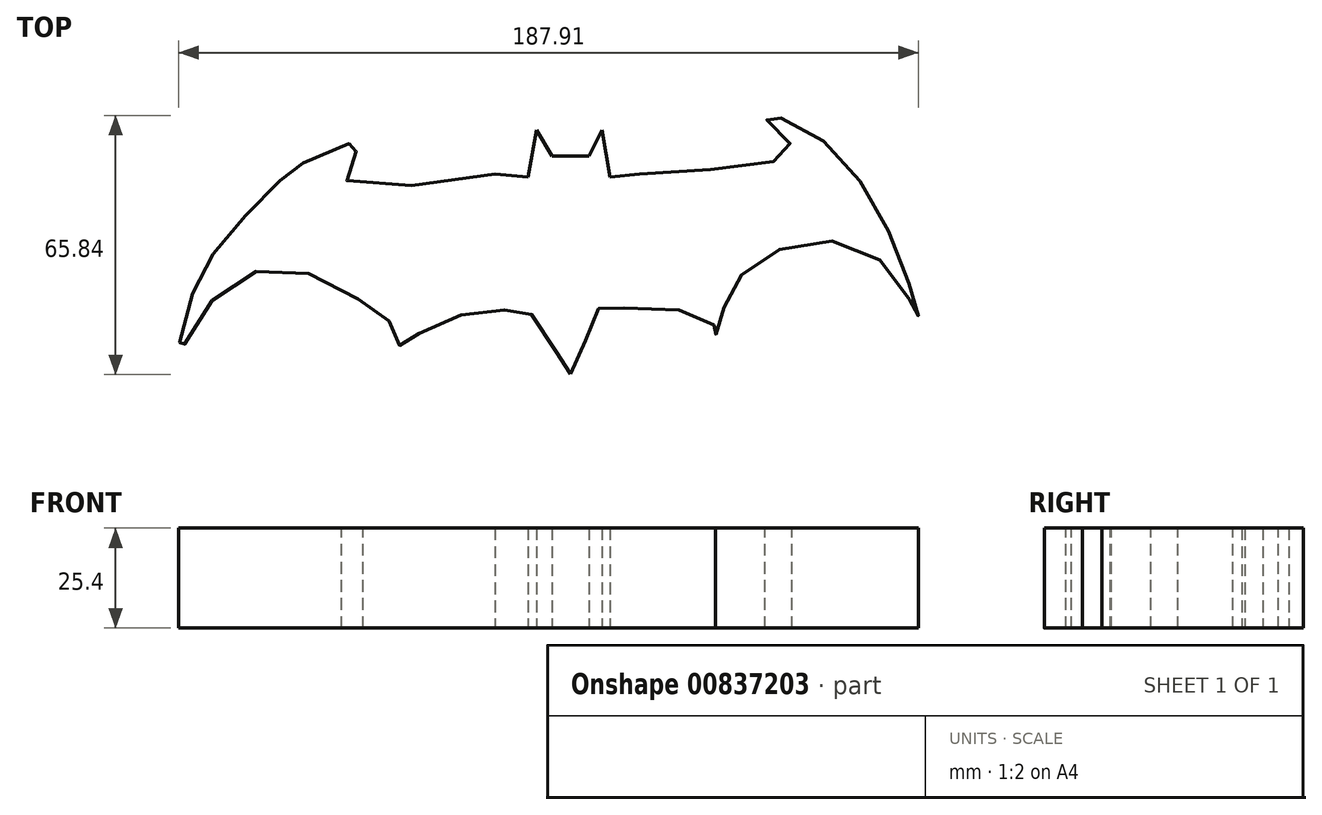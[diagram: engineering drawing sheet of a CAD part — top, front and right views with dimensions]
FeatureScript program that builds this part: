
annotation { "Feature Type Name" : "Feature", "Feature Type Description" : "" }
export const myFeature = defineFeature(function(context is Context, id is Id, definition is map)
    precondition{}
    {
        {
            var Q0;
            Q0=qCreatedBy(makeId("Top.planeOp"),FACE);
            var sketch = newSketch(context, id + "F0", { "sketchPlane" : qUnion([Q0])});
            skLineSegment(sketch, "E0", {"start": v(-13.23, 38.6) * mm, "end": v(-9.33, 32.02) * mm});
            skLineSegment(sketch, "E1", {"start": v(-9.33, 32.02) * mm, "end": v(0, 32.02) * mm});
            skLineSegment(sketch, "E2", {"start": v(0, 32.02) * mm, "end": v(3.35, 38.6) * mm});
            skLineSegment(sketch, "E3", {"start": v(3.35, 38.6) * mm, "end": v(5.33, 26.72) * mm});
            skLineSegment(sketch, "E4", {"start": v(-13.23, 38.6) * mm, "end": v(-15.43, 26.72) * mm});
            skLineSegment(sketch, "E5", {"start": v(-15.43, 26.72) * mm, "end": v(-23.83, 27.38) * mm});
            skLineSegment(sketch, "E6", {"start": v(5.33, 26.72) * mm, "end": v(12.9, 27.38) * mm});
            skPoint(sketch, "E7.13.internal.snap0", {"position": v(-4.67, 32.02) * mm});
            skFitSpline(sketch, "E7", {"points": [v(12.9, 27.38) * mm, v(51.65, 33.72) * mm, v(44.82, 41.77) * mm, v(56.78, 37.87) * mm, v(78.59, 7.04) * mm, v(83.67, -8.84) * mm, v(72.39, 6.9) * mm, v(42.14, 4.94) * mm, v(33.36, -9.45) * mm, v(32.14, -13.84) * mm, v(30.9, -9.7) * mm, v(4.33, -6.53) * mm, v(2.13, -7.26) * mm, v(-4.67, -23.36) * mm, v(-6.9, -20.67) * mm, v(-15.43, -7.5) * mm, v(-22.37, -7.26) * mm, v(-40.23, -10.92) * mm, v(-47.57, -16.67) * mm, v(-49.26, -12.22) * mm, v(-54.95, -6.77) * mm, v(-77.39, 3.48) * mm, v(-97.4, -6.77) * mm, v(-104.08, -18.03) * mm, v(-101.05, -4.09) * mm, v(-92.02, 11.48) * mm, v(-77.41, 26.72) * mm, v(-71.48, 30.74) * mm, v(-57.3, 35.61) * mm, v(-62.75, 27.38) * mm, v(-23.83, 27.38) * mm], "startDerivative": vector(792.2, 72.82) * mm, "endDerivative": vector(750.22, 155.53) * mm});
            skLineSegment(sketch, "E8", {"start": v(-4.67, 32.02) * mm, "end": v(-4.67, -23.36) * mm});
            skSolve(sketch);
        }
        {
            var Q0;
            {var subQ2=sQuery(id+"F0.wireOp",EDGE,"E0");Q0=makeQuery(id+"F0.imprint","IMPRINT",FACE,{"disambiguationData":[TD([[makeQuery(id+"F0.imprint","IMPRINT",EDGE,{"derivedFrom":subQ2}),-1.0]])]});}
            var Q1;
            {var subQ0=sQuery(id+"F0.wireOp",EDGE,"E2");Q1=makeQuery(id+"F0.imprint","IMPRINT",FACE,{"disambiguationData":[TD([[makeQuery(id+"F0.imprint","IMPRINT",EDGE,{"derivedFrom":subQ0}),-1.0]])]});}
            extrude(context, id + "F1", {"entities" : qUnion([Q0, Q1]), "depth" : 25.4 * mm, "offsetDistance" : 25.4 * mm});
        }
    });
